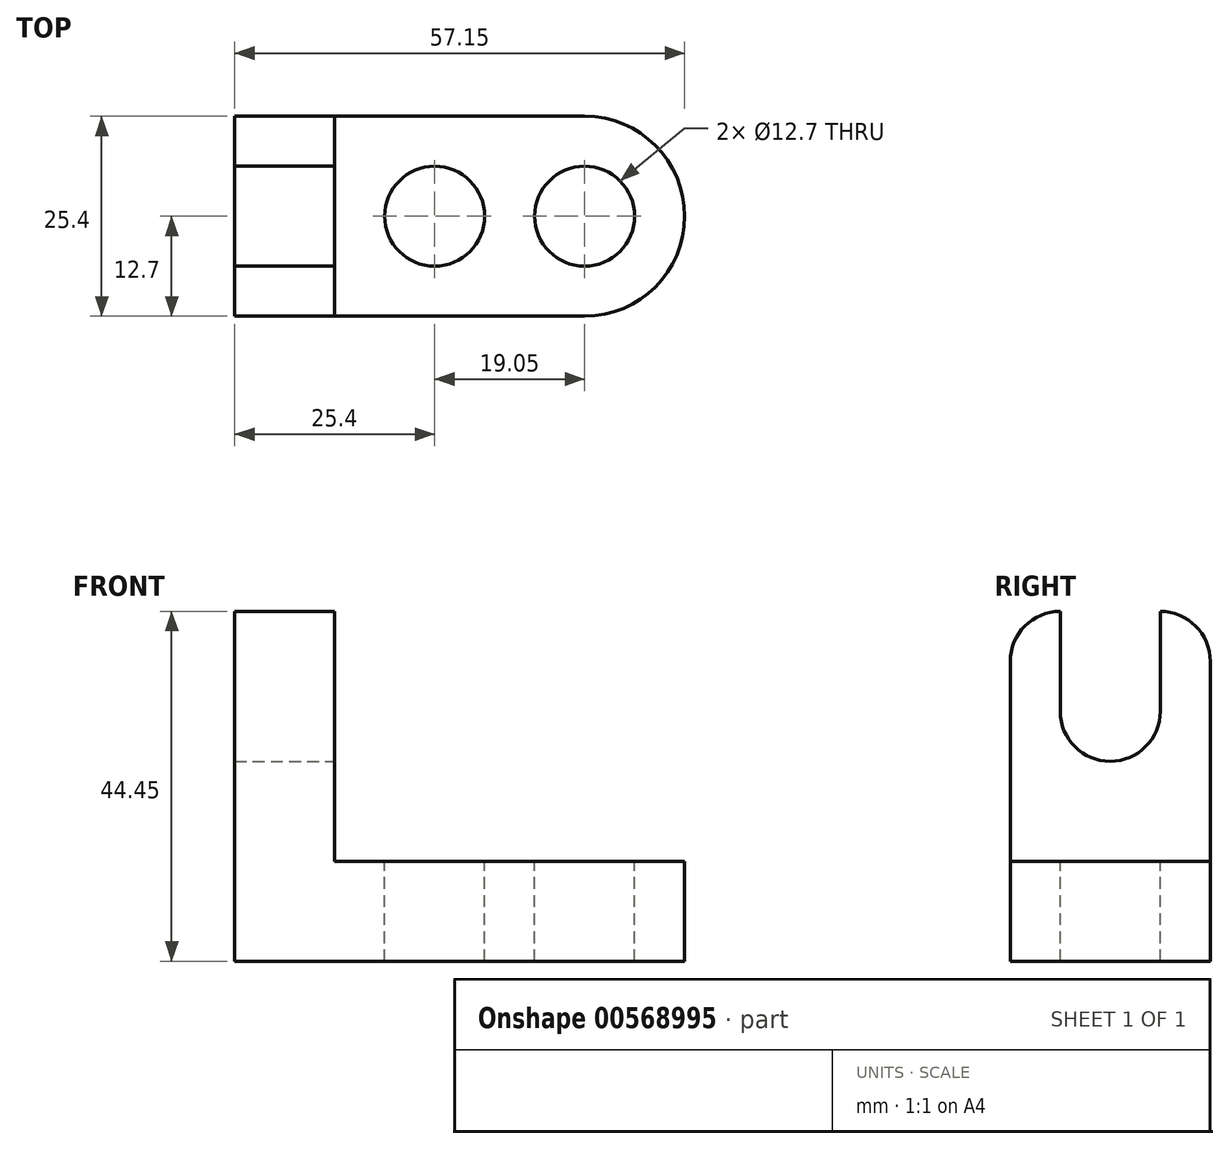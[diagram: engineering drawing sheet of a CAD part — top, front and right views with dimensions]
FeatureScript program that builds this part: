
annotation { "Feature Type Name" : "Feature", "Feature Type Description" : "" }
export const myFeature = defineFeature(function(context is Context, id is Id, definition is map)
    precondition{}
    {
        {
            var Q0;
            Q0=qCreatedBy(makeId("Front.planeOp"),FACE);
            var sketch = newSketch(context, id + "F0", { "sketchPlane" : qUnion([Q0])});
            skLineSegment(sketch, "E0", {"start": v(0, 44.45) * mm, "end": v(0, 0) * mm});
            skLineSegment(sketch, "E1", {"start": v(0, 0) * mm, "end": v(57.15, 0) * mm});
            skLineSegment(sketch, "E2", {"start": v(57.15, 0) * mm, "end": v(57.15, 12.7) * mm});
            skLineSegment(sketch, "E3", {"start": v(0, 44.45) * mm, "end": v(12.7, 44.45) * mm});
            skLineSegment(sketch, "E4", {"start": v(12.7, 44.45) * mm, "end": v(12.7, 12.7) * mm});
            skLineSegment(sketch, "E5", {"start": v(12.7, 12.7) * mm, "end": v(57.15, 12.7) * mm});
            skSolve(sketch);
        }
        {
            var Q0;
            Q0=makeQuery(id+"F0.imprint","IMPRINT",FACE,{"disambiguationData":[TD([[makeQuery(id+"F0.imprint","IMPRINT",EDGE,{"derivedFrom":sQuery(id+"F0.wireOp",EDGE,"E0")}),1.0]])]});
            extrude(context, id + "F1", {"entities" : qUnion([Q0]), "depth" : 25.4 * mm, "offsetDistance" : 25.4 * mm});
        }
        {
            var Q0;
            Q0=makeQuery(id+"F1.opExtrude","SWEPT_FACE",FACE,{"disambiguationData":[OSD([sQuery(id+"F0.wireOp",EDGE,"E5")])]});
            var sketch = newSketch(context, id + "F2", { "sketchPlane" : qUnion([Q0])});
            skCircle(sketch, "E6", {"center": v(25.4, -12.7) * mm, "radius": 6.35 * mm});
            skCircle(sketch, "E7", {"center": v(44.45, -12.7) * mm, "radius": 6.35 * mm});
            skArc(sketch, "E8", {"start": v(44.45, -25.4) * mm, "mid": v(57.15, -12.7) * mm, "end": v(44.45, 0) * mm});
            skSolve(sketch);
        }
        {
            var Q0;
            Q0=makeQuery(id+"F2.imprint","IMPRINT",FACE,{"disambiguationData":[TD([[makeQuery(id+"F2.imprint","IMPRINT",EDGE,{"derivedFrom":sQuery(id+"F2.wireOp",EDGE,"E6")}),1.0]])]});
            var Q1;
            Q1=makeQuery(id+"F2.imprint","IMPRINT",FACE,{"disambiguationData":[TD([[makeQuery(id+"F2.imprint","IMPRINT",EDGE,{"derivedFrom":sQuery(id+"F2.wireOp",EDGE,"E7")}),1.0]])]});
            var Q2;
            {var subQ0=sQuery(id+"F2.wireOp",EDGE,"E8");var subQ1=sQuery(id+"F0.wireOp",EDGE,"E5");var subQ2=makeQuery(id+"F1.opExtrude","CAP_EDGE",EDGE,{"disambiguationData":[OSD([subQ1])],"isStart":false});var subQ3=makeQuery(id+"F2.imprint","INTERSECT",VERTEX,{"derivedFrom":[subQ2,subQ0]});Q2=makeQuery(id+"F2.imprint","IMPRINT",FACE,{"disambiguationData":[TD([[makeQuery(id+"F2.imprint","IMPRINT",EDGE,{"disambiguationData":[TD([[subQ3,-1.0]])],"derivedFrom":subQ0}),-1.0]])]});}
            var Q3;
            {var subQ0=sQuery(id+"F2.wireOp",EDGE,"E8");var subQ1=sQuery(id+"F0.wireOp",EDGE,"E5");var subQ2=makeQuery(id+"F1.opExtrude","CAP_EDGE",EDGE,{"disambiguationData":[OSD([subQ1])],"isStart":true});var subQ3=makeQuery(id+"F2.imprint","INTERSECT",VERTEX,{"derivedFrom":[subQ2,subQ0]});Q3=makeQuery(id+"F2.imprint","IMPRINT",FACE,{"disambiguationData":[TD([[makeQuery(id+"F2.imprint","IMPRINT",EDGE,{"disambiguationData":[TD([[subQ3,1.0]])],"derivedFrom":subQ0}),-1.0]])]});}
            extrude(context, id + "F3", {"entities" : qUnion([Q0, Q1, Q2, Q3]), "operationType" : NewBodyOperationType.REMOVE, "oppositeDirection" : true, "depth" : 12.7 * mm, "offsetDistance" : 25.4 * mm});
        }
        {
            var Q0;
            Q0=makeQuery(id+"F1.opExtrude","SWEPT_FACE",FACE,{"disambiguationData":[OSD([sQuery(id+"F0.wireOp",EDGE,"E4")])]});
            var sketch = newSketch(context, id + "F4", { "sketchPlane" : qUnion([Q0])});
            skLineSegment(sketch, "E9", {"start": v(-19.05, 44.45) * mm, "end": v(-19.05, 31.75) * mm});
            skLineSegment(sketch, "E10", {"start": v(-6.35, 44.45) * mm, "end": v(-6.35, 31.75) * mm});
            skArc(sketch, "E11", {"start": v(-19.05, 31.75) * mm, "mid": v(-12.7, 25.4) * mm, "end": v(-6.35, 31.75) * mm});
            skLineSegment(sketch, "E12", {"start": v(-25.4, 38.1) * mm, "end": v(-25.4, 44.45) * mm});
            skLineSegment(sketch, "E13", {"start": v(-25.4, 44.45) * mm, "end": v(-19.05, 44.45) * mm});
            skLineSegment(sketch, "E14", {"start": v(-6.35, 44.45) * mm, "end": v(0, 44.45) * mm});
            skLineSegment(sketch, "E15", {"start": v(0, 44.45) * mm, "end": v(0, 38.1) * mm});
            skArc(sketch, "E16", {"start": v(-19.05, 44.45) * mm, "mid": v(-23.54, 42.6) * mm, "end": v(-25.4, 38.1) * mm});
            skArc(sketch, "E17", {"start": v(0, 38.1) * mm, "mid": v(-1.86, 42.6) * mm, "end": v(-6.35, 44.45) * mm});
            skSolve(sketch);
        }
        {
            var Q0;
            {var subQ0=sQuery(id+"F4.wireOp",EDGE,"E9");Q0=makeQuery(id+"F4.imprint","IMPRINT",FACE,{"disambiguationData":[TD([[makeQuery(id+"F4.imprint","IMPRINT",EDGE,{"derivedFrom":subQ0}),1.0]])]});}
            var Q1;
            Q1=makeQuery(id+"F4.imprint","IMPRINT",FACE,{"disambiguationData":[TD([[makeQuery(id+"F4.imprint","IMPRINT",EDGE,{"derivedFrom":sQuery(id+"F4.wireOp",EDGE,"E12")}),1.0]])]});
            var Q2;
            Q2=makeQuery(id+"F4.imprint","IMPRINT",FACE,{"disambiguationData":[TD([[makeQuery(id+"F4.imprint","IMPRINT",EDGE,{"derivedFrom":sQuery(id+"F4.wireOp",EDGE,"E14")}),-1.0]])]});
            extrude(context, id + "F5", {"entities" : qUnion([Q0, Q1, Q2]), "operationType" : NewBodyOperationType.REMOVE, "oppositeDirection" : true, "depth" : 12.7 * mm, "offsetDistance" : 25.4 * mm});
        }
    });
